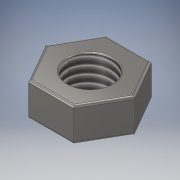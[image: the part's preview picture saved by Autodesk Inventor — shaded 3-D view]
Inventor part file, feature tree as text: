
AUTODESK INVENTOR PART (.ipt)
format: ipt  version: 2018 (Build 220112000, 112)  size: 142,848 bytes
history: native  units: in
note: dims shown in document units (in); Inventor stores cm internally (conversion verified against a paired STEP export)
features: extrude x2, fillet x2, sketch x2, thread x1
ambient origin geometry x8: Origin, YZ Plane, XZ Plane, XY Plane, X Axis, Y Axis, Z Axis, Center Point
bodies: Solid1 (feature_tree)
feature tree (7):
  extrude  "Extrusion1"  Depth=0.1181in TaperAngle=0.0deg
  extrude  "Extrusion2"  Depth=0.1181in TaperAngle=0.0deg
  fillet  "Fillet1"  Radius=0.0079in
  fillet  "Fillet2"  Radius=0.0039in
  thread  "Thread1"  [1 undecoded]
  sketch  "Sketch1"  dims[d0=0.2756in d1=0.1181in d2=0.0in]
  sketch  "Sketch2"  dims[d3=0.1575in d4=0.1181in d5=0.0in d6=0.0079in d7=0.0039in d8=0.3937in d9=0.0in]
note: 1 required parameter value undecoded (feature->parameter linkage not recoverable at this tier; creation-order binding heuristic only, values carry confidence <= 0.55)
